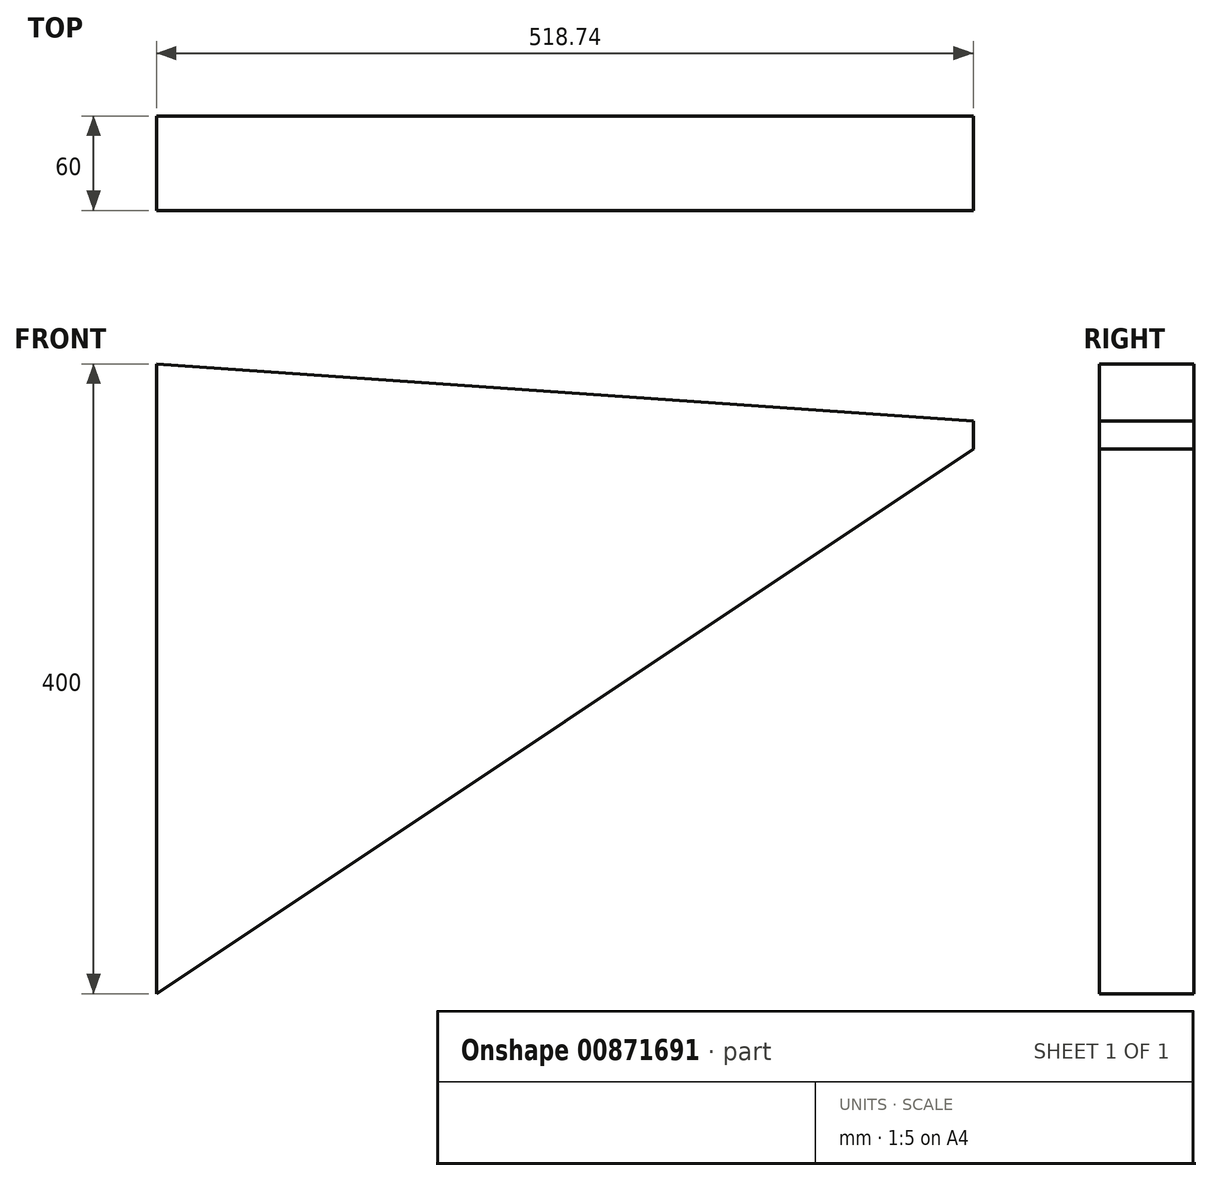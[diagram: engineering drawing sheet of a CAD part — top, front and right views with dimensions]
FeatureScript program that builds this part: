
annotation { "Feature Type Name" : "Feature", "Feature Type Description" : "" }
export const myFeature = defineFeature(function(context is Context, id is Id, definition is map)
    precondition{}
    {
        {
            var Q0;
            Q0=qCreatedBy(makeId("Front.planeOp"),FACE);
            var sketch = newSketch(context, id + "F0", { "sketchPlane" : qUnion([Q0])});
            skLineSegment(sketch, "E0", {"start": v(-372.39, -181.55) * mm, "end": v(146.35, 164.4) * mm});
            skLineSegment(sketch, "E1", {"start": v(-372.39, -181.55) * mm, "end": v(-372.39, 218.45) * mm});
            skLineSegment(sketch, "E2", {"start": v(-372.39, 218.45) * mm, "end": v(146.35, 182.17) * mm});
            skLineSegment(sketch, "E3", {"start": v(146.35, 182.17) * mm, "end": v(146.35, 164.4) * mm});
            skSolve(sketch);
        }
        {
            var Q0;
            Q0 = qSketchRegion(id + "F0", true);
            extrude(context, id + "F1", {"entities" : qUnion([Q0]), "endBound" : BoundingType.SYMMETRIC, "depth" : 60 * mm, "offsetDistance" : 25 * mm});
        }
    });
